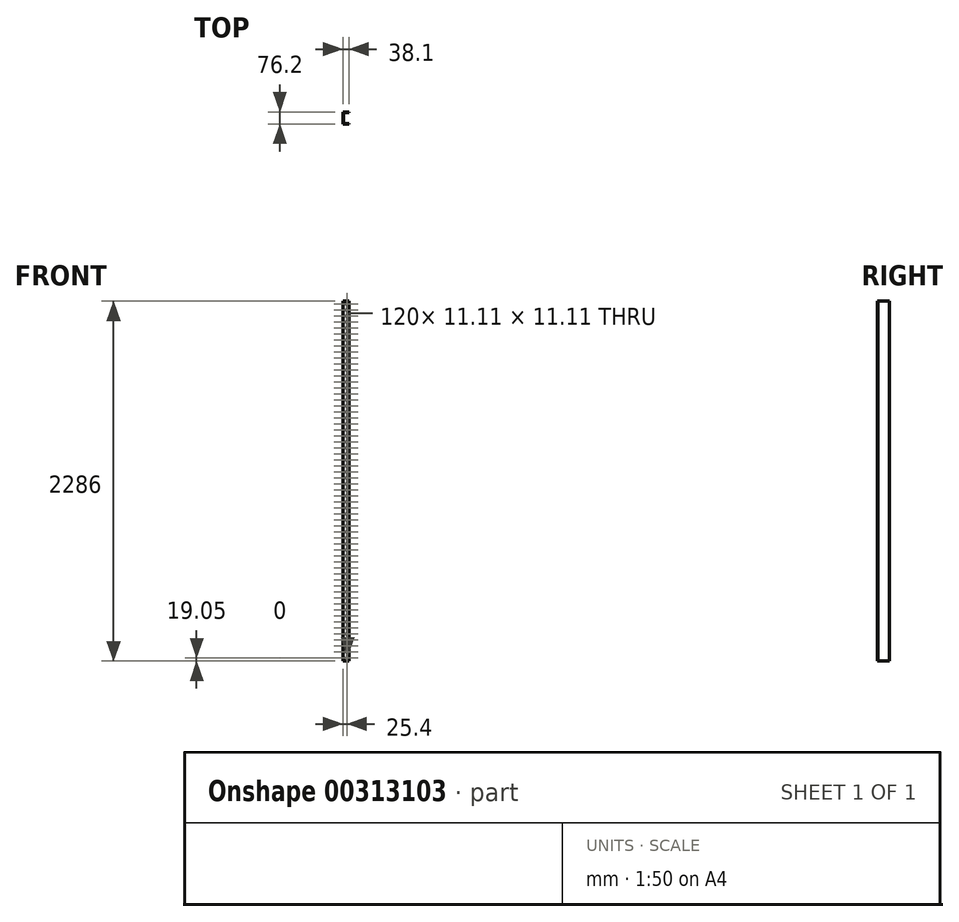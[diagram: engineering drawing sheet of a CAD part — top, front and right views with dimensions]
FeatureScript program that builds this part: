
annotation { "Feature Type Name" : "Feature", "Feature Type Description" : "" }
export const myFeature = defineFeature(function(context is Context, id is Id, definition is map)
    precondition{}
    {
        {
            var Q0;
            Q0=qCreatedBy(makeId("Top.planeOp"),FACE);
            var sketch = newSketch(context, id + "F0", { "sketchPlane" : qUnion([Q0])});
            skLineSegment(sketch, "E0.bottom", {"start": v(0, 0) * mm, "end": v(38.1, 0) * mm});
            skLineSegment(sketch, "E0.top", {"start": v(0, 76.2) * mm, "end": v(38.1, 76.2) * mm});
            skLineSegment(sketch, "E0.left", {"start": v(0, 0) * mm, "end": v(0, 76.2) * mm});
            skLineSegment(sketch, "E0.right", {"start": v(38.1, 0) * mm, "end": v(38.1, 76.2) * mm});
            skSolve(sketch);
        }
        {
            var Q0;
            Q0 = qSketchRegion(id + "F0", true);
            extrude(context, id + "F1", {"entities" : qUnion([Q0]), "endBound" : BoundingType.SYMMETRIC, "depth" : 2286 * mm});
        }
        {
            var Q0;
            Q0=makeQuery(id+"F1.opExtrude","SWEPT_FACE",FACE,{"disambiguationData":[OSD([sQuery(id+"F0.wireOp",EDGE,"E0.right")])]});
            var Q1;
            Q1=makeQuery(id+"F1.opExtrude","CAP_FACE",FACE,{"disambiguationData":[OSD([sQuery(id+"F0.wireOp",EDGE,"E0.bottom"),sQuery(id+"F0.wireOp",EDGE,"E0.top"),sQuery(id+"F0.wireOp",EDGE,"E0.left"),sQuery(id+"F0.wireOp",EDGE,"E0.right")])],"isStart":false});
            var Q2;
            Q2=makeQuery(id+"F1.opExtrude","CAP_FACE",FACE,{"disambiguationData":[OSD([sQuery(id+"F0.wireOp",EDGE,"E0.bottom"),sQuery(id+"F0.wireOp",EDGE,"E0.top"),sQuery(id+"F0.wireOp",EDGE,"E0.left"),sQuery(id+"F0.wireOp",EDGE,"E0.right")])],"isStart":true});
            shell(context, id + "F2", {"entities" : qUnion([Q0, Q1, Q2]), "thickness" : 2.78 * mm});
        }
        {
            var Q0;
            Q0=makeQuery(id+"F1.opExtrude","SWEPT_FACE",FACE,{"disambiguationData":[OSD([sQuery(id+"F0.wireOp",EDGE,"E0.bottom")])]});
            var sketch = newSketch(context, id + "F3", { "sketchPlane" : qUnion([Q0])});
            skLineSegment(sketch, "E1.bottom", {"start": v(30.96, -1118.4) * mm, "end": v(19.84, -1118.4) * mm});
            skLineSegment(sketch, "E1.top", {"start": v(30.96, -1129.5) * mm, "end": v(19.84, -1129.5) * mm});
            skLineSegment(sketch, "E1.left", {"start": v(30.96, -1118.4) * mm, "end": v(30.96, -1129.5) * mm});
            skLineSegment(sketch, "E1.right", {"start": v(19.84, -1118.4) * mm, "end": v(19.84, -1129.5) * mm});
            skPoint(sketch, "E1.middle", {"position": v(25.4, -1123.95) * mm});
            skPoint(sketch, "E1.middle.positionSnap0", {"position": v(19.05, -1143) * mm});
            skPoint(sketch, "E1.centerSnap0", {"position": v(19.05, -1143) * mm});
            skPoint(sketch, "E2.0.1.0", {"position": v(25.4, -1085.85) * mm});
            skLineSegment(sketch, "E2.0.1.1", {"start": v(19.84, -1080.3) * mm, "end": v(19.84, -1091.4) * mm});
            skLineSegment(sketch, "E2.0.1.2", {"start": v(30.96, -1080.3) * mm, "end": v(30.96, -1091.4) * mm});
            skLineSegment(sketch, "E2.0.1.3", {"start": v(30.96, -1091.4) * mm, "end": v(19.84, -1091.4) * mm});
            skLineSegment(sketch, "E2.0.1.4", {"start": v(30.96, -1080.3) * mm, "end": v(19.84, -1080.3) * mm});
            skPoint(sketch, "E2.0.2.0", {"position": v(25.4, -1047.75) * mm});
            skLineSegment(sketch, "E2.0.2.1", {"start": v(19.84, -1042.2) * mm, "end": v(19.84, -1053.3) * mm});
            skLineSegment(sketch, "E2.0.2.2", {"start": v(30.96, -1042.2) * mm, "end": v(30.96, -1053.3) * mm});
            skLineSegment(sketch, "E2.0.2.3", {"start": v(30.96, -1053.3) * mm, "end": v(19.84, -1053.3) * mm});
            skLineSegment(sketch, "E2.0.2.4", {"start": v(30.96, -1042.2) * mm, "end": v(19.84, -1042.2) * mm});
            skPoint(sketch, "E2.0.3.0", {"position": v(25.4, -1009.65) * mm});
            skLineSegment(sketch, "E2.0.3.1", {"start": v(19.84, -1004.1) * mm, "end": v(19.84, -1015.2) * mm});
            skLineSegment(sketch, "E2.0.3.2", {"start": v(30.96, -1004.1) * mm, "end": v(30.96, -1015.2) * mm});
            skLineSegment(sketch, "E2.0.3.3", {"start": v(30.96, -1015.2) * mm, "end": v(19.84, -1015.2) * mm});
            skLineSegment(sketch, "E2.0.3.4", {"start": v(30.96, -1004.1) * mm, "end": v(19.84, -1004.1) * mm});
            skPoint(sketch, "E2.0.4.0", {"position": v(25.4, -971.55) * mm});
            skLineSegment(sketch, "E2.0.4.1", {"start": v(19.84, -966) * mm, "end": v(19.84, -977.1) * mm});
            skLineSegment(sketch, "E2.0.4.2", {"start": v(30.96, -966) * mm, "end": v(30.96, -977.1) * mm});
            skLineSegment(sketch, "E2.0.4.3", {"start": v(30.96, -977.1) * mm, "end": v(19.84, -977.1) * mm});
            skLineSegment(sketch, "E2.0.4.4", {"start": v(30.96, -966) * mm, "end": v(19.84, -966) * mm});
            skPoint(sketch, "E2.0.5.0", {"position": v(25.4, -933.45) * mm});
            skLineSegment(sketch, "E2.0.5.1", {"start": v(19.84, -927.9) * mm, "end": v(19.84, -939) * mm});
            skLineSegment(sketch, "E2.0.5.2", {"start": v(30.96, -927.9) * mm, "end": v(30.96, -939) * mm});
            skLineSegment(sketch, "E2.0.5.3", {"start": v(30.96, -939) * mm, "end": v(19.84, -939) * mm});
            skLineSegment(sketch, "E2.0.5.4", {"start": v(30.96, -927.9) * mm, "end": v(19.84, -927.9) * mm});
            skPoint(sketch, "E2.0.6.0", {"position": v(25.4, -895.35) * mm});
            skLineSegment(sketch, "E2.0.6.1", {"start": v(19.84, -889.8) * mm, "end": v(19.84, -900.9) * mm});
            skLineSegment(sketch, "E2.0.6.2", {"start": v(30.96, -889.8) * mm, "end": v(30.96, -900.9) * mm});
            skLineSegment(sketch, "E2.0.6.3", {"start": v(30.96, -900.9) * mm, "end": v(19.84, -900.9) * mm});
            skLineSegment(sketch, "E2.0.6.4", {"start": v(30.96, -889.8) * mm, "end": v(19.84, -889.8) * mm});
            skPoint(sketch, "E2.0.7.0", {"position": v(25.4, -857.25) * mm});
            skLineSegment(sketch, "E2.0.7.1", {"start": v(19.84, -851.7) * mm, "end": v(19.84, -862.8) * mm});
            skLineSegment(sketch, "E2.0.7.2", {"start": v(30.96, -851.7) * mm, "end": v(30.96, -862.8) * mm});
            skLineSegment(sketch, "E2.0.7.3", {"start": v(30.96, -862.8) * mm, "end": v(19.84, -862.8) * mm});
            skLineSegment(sketch, "E2.0.7.4", {"start": v(30.96, -851.7) * mm, "end": v(19.84, -851.7) * mm});
            skPoint(sketch, "E2.0.8.0", {"position": v(25.4, -819.15) * mm});
            skLineSegment(sketch, "E2.0.8.1", {"start": v(19.84, -813.6) * mm, "end": v(19.84, -824.7) * mm});
            skLineSegment(sketch, "E2.0.8.2", {"start": v(30.96, -813.6) * mm, "end": v(30.96, -824.7) * mm});
            skLineSegment(sketch, "E2.0.8.3", {"start": v(30.96, -824.7) * mm, "end": v(19.84, -824.7) * mm});
            skLineSegment(sketch, "E2.0.8.4", {"start": v(30.96, -813.6) * mm, "end": v(19.84, -813.6) * mm});
            skPoint(sketch, "E2.0.9.0", {"position": v(25.4, -781.05) * mm});
            skLineSegment(sketch, "E2.0.9.1", {"start": v(19.84, -775.5) * mm, "end": v(19.84, -786.6) * mm});
            skLineSegment(sketch, "E2.0.9.2", {"start": v(30.96, -775.5) * mm, "end": v(30.96, -786.6) * mm});
            skLineSegment(sketch, "E2.0.9.3", {"start": v(30.96, -786.6) * mm, "end": v(19.84, -786.6) * mm});
            skLineSegment(sketch, "E2.0.9.4", {"start": v(30.96, -775.5) * mm, "end": v(19.84, -775.5) * mm});
            skPoint(sketch, "E2.0.10.0", {"position": v(25.4, -742.95) * mm});
            skLineSegment(sketch, "E2.0.10.1", {"start": v(19.84, -737.4) * mm, "end": v(19.84, -748.5) * mm});
            skLineSegment(sketch, "E2.0.10.2", {"start": v(30.96, -737.4) * mm, "end": v(30.96, -748.5) * mm});
            skLineSegment(sketch, "E2.0.10.3", {"start": v(30.96, -748.5) * mm, "end": v(19.84, -748.5) * mm});
            skLineSegment(sketch, "E2.0.10.4", {"start": v(30.96, -737.4) * mm, "end": v(19.84, -737.4) * mm});
            skPoint(sketch, "E2.0.11.0", {"position": v(25.4, -704.85) * mm});
            skLineSegment(sketch, "E2.0.11.1", {"start": v(19.84, -699.3) * mm, "end": v(19.84, -710.4) * mm});
            skLineSegment(sketch, "E2.0.11.2", {"start": v(30.96, -699.3) * mm, "end": v(30.96, -710.4) * mm});
            skLineSegment(sketch, "E2.0.11.3", {"start": v(30.96, -710.4) * mm, "end": v(19.84, -710.4) * mm});
            skLineSegment(sketch, "E2.0.11.4", {"start": v(30.96, -699.3) * mm, "end": v(19.84, -699.3) * mm});
            skPoint(sketch, "E2.0.12.0", {"position": v(25.4, -666.75) * mm});
            skLineSegment(sketch, "E2.0.12.1", {"start": v(19.84, -661.2) * mm, "end": v(19.84, -672.3) * mm});
            skLineSegment(sketch, "E2.0.12.2", {"start": v(30.96, -661.2) * mm, "end": v(30.96, -672.3) * mm});
            skLineSegment(sketch, "E2.0.12.3", {"start": v(30.96, -672.3) * mm, "end": v(19.84, -672.3) * mm});
            skLineSegment(sketch, "E2.0.12.4", {"start": v(30.96, -661.2) * mm, "end": v(19.84, -661.2) * mm});
            skPoint(sketch, "E2.0.13.0", {"position": v(25.4, -628.65) * mm});
            skLineSegment(sketch, "E2.0.13.1", {"start": v(19.84, -623.1) * mm, "end": v(19.84, -634.2) * mm});
            skLineSegment(sketch, "E2.0.13.2", {"start": v(30.96, -623.1) * mm, "end": v(30.96, -634.2) * mm});
            skLineSegment(sketch, "E2.0.13.3", {"start": v(30.96, -634.2) * mm, "end": v(19.84, -634.2) * mm});
            skLineSegment(sketch, "E2.0.13.4", {"start": v(30.96, -623.1) * mm, "end": v(19.84, -623.1) * mm});
            skPoint(sketch, "E2.0.14.0", {"position": v(25.4, -590.55) * mm});
            skLineSegment(sketch, "E2.0.14.1", {"start": v(19.84, -585) * mm, "end": v(19.84, -596.1) * mm});
            skLineSegment(sketch, "E2.0.14.2", {"start": v(30.96, -585) * mm, "end": v(30.96, -596.1) * mm});
            skLineSegment(sketch, "E2.0.14.3", {"start": v(30.96, -596.1) * mm, "end": v(19.84, -596.1) * mm});
            skLineSegment(sketch, "E2.0.14.4", {"start": v(30.96, -585) * mm, "end": v(19.84, -585) * mm});
            skPoint(sketch, "E2.0.15.0", {"position": v(25.4, -552.45) * mm});
            skLineSegment(sketch, "E2.0.15.1", {"start": v(19.84, -546.9) * mm, "end": v(19.84, -558) * mm});
            skLineSegment(sketch, "E2.0.15.2", {"start": v(30.96, -546.9) * mm, "end": v(30.96, -558) * mm});
            skLineSegment(sketch, "E2.0.15.3", {"start": v(30.96, -558) * mm, "end": v(19.84, -558) * mm});
            skLineSegment(sketch, "E2.0.15.4", {"start": v(30.96, -546.9) * mm, "end": v(19.84, -546.9) * mm});
            skPoint(sketch, "E2.0.16.0", {"position": v(25.4, -514.35) * mm});
            skLineSegment(sketch, "E2.0.16.1", {"start": v(19.84, -508.8) * mm, "end": v(19.84, -519.9) * mm});
            skLineSegment(sketch, "E2.0.16.2", {"start": v(30.96, -508.8) * mm, "end": v(30.96, -519.9) * mm});
            skLineSegment(sketch, "E2.0.16.3", {"start": v(30.96, -519.9) * mm, "end": v(19.84, -519.9) * mm});
            skLineSegment(sketch, "E2.0.16.4", {"start": v(30.96, -508.8) * mm, "end": v(19.84, -508.8) * mm});
            skPoint(sketch, "E2.0.17.0", {"position": v(25.4, -476.25) * mm});
            skLineSegment(sketch, "E2.0.17.1", {"start": v(19.84, -470.7) * mm, "end": v(19.84, -481.8) * mm});
            skLineSegment(sketch, "E2.0.17.2", {"start": v(30.96, -470.7) * mm, "end": v(30.96, -481.8) * mm});
            skLineSegment(sketch, "E2.0.17.3", {"start": v(30.96, -481.8) * mm, "end": v(19.84, -481.8) * mm});
            skLineSegment(sketch, "E2.0.17.4", {"start": v(30.96, -470.7) * mm, "end": v(19.84, -470.7) * mm});
            skPoint(sketch, "E2.0.18.0", {"position": v(25.4, -438.15) * mm});
            skLineSegment(sketch, "E2.0.18.1", {"start": v(19.84, -432.6) * mm, "end": v(19.84, -443.7) * mm});
            skLineSegment(sketch, "E2.0.18.2", {"start": v(30.96, -432.6) * mm, "end": v(30.96, -443.7) * mm});
            skLineSegment(sketch, "E2.0.18.3", {"start": v(30.96, -443.7) * mm, "end": v(19.84, -443.7) * mm});
            skLineSegment(sketch, "E2.0.18.4", {"start": v(30.96, -432.6) * mm, "end": v(19.84, -432.6) * mm});
            skPoint(sketch, "E2.0.19.0", {"position": v(25.4, -400.05) * mm});
            skLineSegment(sketch, "E2.0.19.1", {"start": v(19.84, -394.5) * mm, "end": v(19.84, -405.6) * mm});
            skLineSegment(sketch, "E2.0.19.2", {"start": v(30.96, -394.5) * mm, "end": v(30.96, -405.6) * mm});
            skLineSegment(sketch, "E2.0.19.3", {"start": v(30.96, -405.6) * mm, "end": v(19.84, -405.6) * mm});
            skLineSegment(sketch, "E2.0.19.4", {"start": v(30.96, -394.5) * mm, "end": v(19.84, -394.5) * mm});
            skPoint(sketch, "E2.0.20.0", {"position": v(25.4, -361.95) * mm});
            skLineSegment(sketch, "E2.0.20.1", {"start": v(19.84, -356.4) * mm, "end": v(19.84, -367.5) * mm});
            skLineSegment(sketch, "E2.0.20.2", {"start": v(30.96, -356.4) * mm, "end": v(30.96, -367.5) * mm});
            skLineSegment(sketch, "E2.0.20.3", {"start": v(30.96, -367.5) * mm, "end": v(19.84, -367.5) * mm});
            skLineSegment(sketch, "E2.0.20.4", {"start": v(30.96, -356.4) * mm, "end": v(19.84, -356.4) * mm});
            skPoint(sketch, "E2.0.21.0", {"position": v(25.4, -323.85) * mm});
            skLineSegment(sketch, "E2.0.21.1", {"start": v(19.84, -318.3) * mm, "end": v(19.84, -329.4) * mm});
            skLineSegment(sketch, "E2.0.21.2", {"start": v(30.96, -318.3) * mm, "end": v(30.96, -329.4) * mm});
            skLineSegment(sketch, "E2.0.21.3", {"start": v(30.96, -329.4) * mm, "end": v(19.84, -329.4) * mm});
            skLineSegment(sketch, "E2.0.21.4", {"start": v(30.96, -318.3) * mm, "end": v(19.84, -318.3) * mm});
            skPoint(sketch, "E2.0.22.0", {"position": v(25.4, -285.75) * mm});
            skLineSegment(sketch, "E2.0.22.1", {"start": v(19.84, -280.2) * mm, "end": v(19.84, -291.3) * mm});
            skLineSegment(sketch, "E2.0.22.2", {"start": v(30.96, -280.2) * mm, "end": v(30.96, -291.3) * mm});
            skLineSegment(sketch, "E2.0.22.3", {"start": v(30.96, -291.3) * mm, "end": v(19.84, -291.3) * mm});
            skLineSegment(sketch, "E2.0.22.4", {"start": v(30.96, -280.2) * mm, "end": v(19.84, -280.2) * mm});
            skPoint(sketch, "E2.0.23.0", {"position": v(25.4, -247.65) * mm});
            skLineSegment(sketch, "E2.0.23.1", {"start": v(19.84, -242.1) * mm, "end": v(19.84, -253.2) * mm});
            skLineSegment(sketch, "E2.0.23.2", {"start": v(30.96, -242.1) * mm, "end": v(30.96, -253.2) * mm});
            skLineSegment(sketch, "E2.0.23.3", {"start": v(30.96, -253.2) * mm, "end": v(19.84, -253.2) * mm});
            skLineSegment(sketch, "E2.0.23.4", {"start": v(30.96, -242.1) * mm, "end": v(19.84, -242.1) * mm});
            skPoint(sketch, "E2.0.24.0", {"position": v(25.4, -209.55) * mm});
            skLineSegment(sketch, "E2.0.24.1", {"start": v(19.84, -204) * mm, "end": v(19.84, -215.1) * mm});
            skLineSegment(sketch, "E2.0.24.2", {"start": v(30.96, -204) * mm, "end": v(30.96, -215.1) * mm});
            skLineSegment(sketch, "E2.0.24.3", {"start": v(30.96, -215.1) * mm, "end": v(19.84, -215.1) * mm});
            skLineSegment(sketch, "E2.0.24.4", {"start": v(30.96, -204) * mm, "end": v(19.84, -204) * mm});
            skPoint(sketch, "E2.0.25.0", {"position": v(25.4, -171.45) * mm});
            skLineSegment(sketch, "E2.0.25.1", {"start": v(19.84, -165.9) * mm, "end": v(19.84, -177) * mm});
            skLineSegment(sketch, "E2.0.25.2", {"start": v(30.96, -165.9) * mm, "end": v(30.96, -177) * mm});
            skLineSegment(sketch, "E2.0.25.3", {"start": v(30.96, -177) * mm, "end": v(19.84, -177) * mm});
            skLineSegment(sketch, "E2.0.25.4", {"start": v(30.96, -165.9) * mm, "end": v(19.84, -165.9) * mm});
            skPoint(sketch, "E2.0.26.0", {"position": v(25.4, -133.35) * mm});
            skLineSegment(sketch, "E2.0.26.1", {"start": v(19.84, -127.8) * mm, "end": v(19.84, -138.9) * mm});
            skLineSegment(sketch, "E2.0.26.2", {"start": v(30.96, -127.8) * mm, "end": v(30.96, -138.9) * mm});
            skLineSegment(sketch, "E2.0.26.3", {"start": v(30.96, -138.9) * mm, "end": v(19.84, -138.9) * mm});
            skLineSegment(sketch, "E2.0.26.4", {"start": v(30.96, -127.8) * mm, "end": v(19.84, -127.8) * mm});
            skPoint(sketch, "E2.0.27.0", {"position": v(25.4, -95.25) * mm});
            skLineSegment(sketch, "E2.0.27.1", {"start": v(19.84, -89.7) * mm, "end": v(19.84, -100.8) * mm});
            skLineSegment(sketch, "E2.0.27.2", {"start": v(30.96, -89.7) * mm, "end": v(30.96, -100.8) * mm});
            skLineSegment(sketch, "E2.0.27.3", {"start": v(30.96, -100.8) * mm, "end": v(19.84, -100.8) * mm});
            skLineSegment(sketch, "E2.0.27.4", {"start": v(30.96, -89.7) * mm, "end": v(19.84, -89.7) * mm});
            skPoint(sketch, "E2.0.28.0", {"position": v(25.4, -57.15) * mm});
            skLineSegment(sketch, "E2.0.28.1", {"start": v(19.84, -51.6) * mm, "end": v(19.84, -62.7) * mm});
            skLineSegment(sketch, "E2.0.28.2", {"start": v(30.96, -51.6) * mm, "end": v(30.96, -62.7) * mm});
            skLineSegment(sketch, "E2.0.28.3", {"start": v(30.96, -62.7) * mm, "end": v(19.84, -62.7) * mm});
            skLineSegment(sketch, "E2.0.28.4", {"start": v(30.96, -51.6) * mm, "end": v(19.84, -51.6) * mm});
            skPoint(sketch, "E2.0.29.0", {"position": v(25.4, -19.05) * mm});
            skLineSegment(sketch, "E2.0.29.1", {"start": v(19.84, -13.5) * mm, "end": v(19.84, -24.6) * mm});
            skLineSegment(sketch, "E2.0.29.2", {"start": v(30.96, -13.5) * mm, "end": v(30.96, -24.6) * mm});
            skLineSegment(sketch, "E2.0.29.3", {"start": v(30.96, -24.6) * mm, "end": v(19.84, -24.6) * mm});
            skLineSegment(sketch, "E2.0.29.4", {"start": v(30.96, -13.5) * mm, "end": v(19.84, -13.5) * mm});
            skPoint(sketch, "E2.0.30.0", {"position": v(25.4, 19.05) * mm});
            skLineSegment(sketch, "E2.0.30.1", {"start": v(19.84, 24.6) * mm, "end": v(19.84, 13.5) * mm});
            skLineSegment(sketch, "E2.0.30.2", {"start": v(30.96, 24.6) * mm, "end": v(30.96, 13.5) * mm});
            skLineSegment(sketch, "E2.0.30.3", {"start": v(30.96, 13.5) * mm, "end": v(19.84, 13.5) * mm});
            skLineSegment(sketch, "E2.0.30.4", {"start": v(30.96, 24.6) * mm, "end": v(19.84, 24.6) * mm});
            skPoint(sketch, "E2.0.31.0", {"position": v(25.4, 57.15) * mm});
            skLineSegment(sketch, "E2.0.31.1", {"start": v(19.84, 62.7) * mm, "end": v(19.84, 51.6) * mm});
            skLineSegment(sketch, "E2.0.31.2", {"start": v(30.96, 62.7) * mm, "end": v(30.96, 51.6) * mm});
            skLineSegment(sketch, "E2.0.31.3", {"start": v(30.96, 51.6) * mm, "end": v(19.84, 51.6) * mm});
            skLineSegment(sketch, "E2.0.31.4", {"start": v(30.96, 62.7) * mm, "end": v(19.84, 62.7) * mm});
            skPoint(sketch, "E2.0.32.0", {"position": v(25.4, 95.25) * mm});
            skLineSegment(sketch, "E2.0.32.1", {"start": v(19.84, 100.8) * mm, "end": v(19.84, 89.7) * mm});
            skLineSegment(sketch, "E2.0.32.2", {"start": v(30.96, 100.8) * mm, "end": v(30.96, 89.7) * mm});
            skLineSegment(sketch, "E2.0.32.3", {"start": v(30.96, 89.7) * mm, "end": v(19.84, 89.7) * mm});
            skLineSegment(sketch, "E2.0.32.4", {"start": v(30.96, 100.8) * mm, "end": v(19.84, 100.8) * mm});
            skPoint(sketch, "E2.0.33.0", {"position": v(25.4, 133.35) * mm});
            skLineSegment(sketch, "E2.0.33.1", {"start": v(19.84, 138.9) * mm, "end": v(19.84, 127.8) * mm});
            skLineSegment(sketch, "E2.0.33.2", {"start": v(30.96, 138.9) * mm, "end": v(30.96, 127.8) * mm});
            skLineSegment(sketch, "E2.0.33.3", {"start": v(30.96, 127.8) * mm, "end": v(19.84, 127.8) * mm});
            skLineSegment(sketch, "E2.0.33.4", {"start": v(30.96, 138.9) * mm, "end": v(19.84, 138.9) * mm});
            skPoint(sketch, "E2.0.34.0", {"position": v(25.4, 171.45) * mm});
            skLineSegment(sketch, "E2.0.34.1", {"start": v(19.84, 177) * mm, "end": v(19.84, 165.9) * mm});
            skLineSegment(sketch, "E2.0.34.2", {"start": v(30.96, 177) * mm, "end": v(30.96, 165.9) * mm});
            skLineSegment(sketch, "E2.0.34.3", {"start": v(30.96, 165.9) * mm, "end": v(19.84, 165.9) * mm});
            skLineSegment(sketch, "E2.0.34.4", {"start": v(30.96, 177) * mm, "end": v(19.84, 177) * mm});
            skPoint(sketch, "E2.0.35.0", {"position": v(25.4, 209.55) * mm});
            skLineSegment(sketch, "E2.0.35.1", {"start": v(19.84, 215.1) * mm, "end": v(19.84, 204) * mm});
            skLineSegment(sketch, "E2.0.35.2", {"start": v(30.96, 215.1) * mm, "end": v(30.96, 204) * mm});
            skLineSegment(sketch, "E2.0.35.3", {"start": v(30.96, 204) * mm, "end": v(19.84, 204) * mm});
            skLineSegment(sketch, "E2.0.35.4", {"start": v(30.96, 215.1) * mm, "end": v(19.84, 215.1) * mm});
            skPoint(sketch, "E2.0.36.0", {"position": v(25.4, 247.65) * mm});
            skLineSegment(sketch, "E2.0.36.1", {"start": v(19.84, 253.2) * mm, "end": v(19.84, 242.1) * mm});
            skLineSegment(sketch, "E2.0.36.2", {"start": v(30.96, 253.2) * mm, "end": v(30.96, 242.1) * mm});
            skLineSegment(sketch, "E2.0.36.3", {"start": v(30.96, 242.1) * mm, "end": v(19.84, 242.1) * mm});
            skLineSegment(sketch, "E2.0.36.4", {"start": v(30.96, 253.2) * mm, "end": v(19.84, 253.2) * mm});
            skPoint(sketch, "E2.0.37.0", {"position": v(25.4, 285.75) * mm});
            skLineSegment(sketch, "E2.0.37.1", {"start": v(19.84, 291.3) * mm, "end": v(19.84, 280.2) * mm});
            skLineSegment(sketch, "E2.0.37.2", {"start": v(30.96, 291.3) * mm, "end": v(30.96, 280.2) * mm});
            skLineSegment(sketch, "E2.0.37.3", {"start": v(30.96, 280.2) * mm, "end": v(19.84, 280.2) * mm});
            skLineSegment(sketch, "E2.0.37.4", {"start": v(30.96, 291.3) * mm, "end": v(19.84, 291.3) * mm});
            skPoint(sketch, "E2.0.38.0", {"position": v(25.4, 323.85) * mm});
            skLineSegment(sketch, "E2.0.38.1", {"start": v(19.84, 329.4) * mm, "end": v(19.84, 318.3) * mm});
            skLineSegment(sketch, "E2.0.38.2", {"start": v(30.96, 329.4) * mm, "end": v(30.96, 318.3) * mm});
            skLineSegment(sketch, "E2.0.38.3", {"start": v(30.96, 318.3) * mm, "end": v(19.84, 318.3) * mm});
            skLineSegment(sketch, "E2.0.38.4", {"start": v(30.96, 329.4) * mm, "end": v(19.84, 329.4) * mm});
            skPoint(sketch, "E2.0.39.0", {"position": v(25.4, 361.95) * mm});
            skLineSegment(sketch, "E2.0.39.1", {"start": v(19.84, 367.5) * mm, "end": v(19.84, 356.4) * mm});
            skLineSegment(sketch, "E2.0.39.2", {"start": v(30.96, 367.5) * mm, "end": v(30.96, 356.4) * mm});
            skLineSegment(sketch, "E2.0.39.3", {"start": v(30.96, 356.4) * mm, "end": v(19.84, 356.4) * mm});
            skLineSegment(sketch, "E2.0.39.4", {"start": v(30.96, 367.5) * mm, "end": v(19.84, 367.5) * mm});
            skPoint(sketch, "E2.0.40.0", {"position": v(25.4, 400.05) * mm});
            skLineSegment(sketch, "E2.0.40.1", {"start": v(19.84, 405.6) * mm, "end": v(19.84, 394.5) * mm});
            skLineSegment(sketch, "E2.0.40.2", {"start": v(30.96, 405.6) * mm, "end": v(30.96, 394.5) * mm});
            skLineSegment(sketch, "E2.0.40.3", {"start": v(30.96, 394.5) * mm, "end": v(19.84, 394.5) * mm});
            skLineSegment(sketch, "E2.0.40.4", {"start": v(30.96, 405.6) * mm, "end": v(19.84, 405.6) * mm});
            skPoint(sketch, "E2.0.41.0", {"position": v(25.4, 438.15) * mm});
            skLineSegment(sketch, "E2.0.41.1", {"start": v(19.84, 443.7) * mm, "end": v(19.84, 432.6) * mm});
            skLineSegment(sketch, "E2.0.41.2", {"start": v(30.96, 443.7) * mm, "end": v(30.96, 432.6) * mm});
            skLineSegment(sketch, "E2.0.41.3", {"start": v(30.96, 432.6) * mm, "end": v(19.84, 432.6) * mm});
            skLineSegment(sketch, "E2.0.41.4", {"start": v(30.96, 443.7) * mm, "end": v(19.84, 443.7) * mm});
            skPoint(sketch, "E2.0.42.0", {"position": v(25.4, 476.25) * mm});
            skLineSegment(sketch, "E2.0.42.1", {"start": v(19.84, 481.8) * mm, "end": v(19.84, 470.7) * mm});
            skLineSegment(sketch, "E2.0.42.2", {"start": v(30.96, 481.8) * mm, "end": v(30.96, 470.7) * mm});
            skLineSegment(sketch, "E2.0.42.3", {"start": v(30.96, 470.7) * mm, "end": v(19.84, 470.7) * mm});
            skLineSegment(sketch, "E2.0.42.4", {"start": v(30.96, 481.8) * mm, "end": v(19.84, 481.8) * mm});
            skPoint(sketch, "E2.0.43.0", {"position": v(25.4, 514.35) * mm});
            skLineSegment(sketch, "E2.0.43.1", {"start": v(19.84, 519.9) * mm, "end": v(19.84, 508.8) * mm});
            skLineSegment(sketch, "E2.0.43.2", {"start": v(30.96, 519.9) * mm, "end": v(30.96, 508.8) * mm});
            skLineSegment(sketch, "E2.0.43.3", {"start": v(30.96, 508.8) * mm, "end": v(19.84, 508.8) * mm});
            skLineSegment(sketch, "E2.0.43.4", {"start": v(30.96, 519.9) * mm, "end": v(19.84, 519.9) * mm});
            skPoint(sketch, "E2.0.44.0", {"position": v(25.4, 552.45) * mm});
            skLineSegment(sketch, "E2.0.44.1", {"start": v(19.84, 558) * mm, "end": v(19.84, 546.9) * mm});
            skLineSegment(sketch, "E2.0.44.2", {"start": v(30.96, 558) * mm, "end": v(30.96, 546.9) * mm});
            skLineSegment(sketch, "E2.0.44.3", {"start": v(30.96, 546.9) * mm, "end": v(19.84, 546.9) * mm});
            skLineSegment(sketch, "E2.0.44.4", {"start": v(30.96, 558) * mm, "end": v(19.84, 558) * mm});
            skPoint(sketch, "E2.0.45.0", {"position": v(25.4, 590.55) * mm});
            skLineSegment(sketch, "E2.0.45.1", {"start": v(19.84, 596.1) * mm, "end": v(19.84, 585) * mm});
            skLineSegment(sketch, "E2.0.45.2", {"start": v(30.96, 596.1) * mm, "end": v(30.96, 585) * mm});
            skLineSegment(sketch, "E2.0.45.3", {"start": v(30.96, 585) * mm, "end": v(19.84, 585) * mm});
            skLineSegment(sketch, "E2.0.45.4", {"start": v(30.96, 596.1) * mm, "end": v(19.84, 596.1) * mm});
            skPoint(sketch, "E2.0.46.0", {"position": v(25.4, 628.65) * mm});
            skLineSegment(sketch, "E2.0.46.1", {"start": v(19.84, 634.2) * mm, "end": v(19.84, 623.1) * mm});
            skLineSegment(sketch, "E2.0.46.2", {"start": v(30.96, 634.2) * mm, "end": v(30.96, 623.1) * mm});
            skLineSegment(sketch, "E2.0.46.3", {"start": v(30.96, 623.1) * mm, "end": v(19.84, 623.1) * mm});
            skLineSegment(sketch, "E2.0.46.4", {"start": v(30.96, 634.2) * mm, "end": v(19.84, 634.2) * mm});
            skPoint(sketch, "E2.0.47.0", {"position": v(25.4, 666.75) * mm});
            skLineSegment(sketch, "E2.0.47.1", {"start": v(19.84, 672.3) * mm, "end": v(19.84, 661.2) * mm});
            skLineSegment(sketch, "E2.0.47.2", {"start": v(30.96, 672.3) * mm, "end": v(30.96, 661.2) * mm});
            skLineSegment(sketch, "E2.0.47.3", {"start": v(30.96, 661.2) * mm, "end": v(19.84, 661.2) * mm});
            skLineSegment(sketch, "E2.0.47.4", {"start": v(30.96, 672.3) * mm, "end": v(19.84, 672.3) * mm});
            skPoint(sketch, "E2.0.48.0", {"position": v(25.4, 704.85) * mm});
            skLineSegment(sketch, "E2.0.48.1", {"start": v(19.84, 710.4) * mm, "end": v(19.84, 699.3) * mm});
            skLineSegment(sketch, "E2.0.48.2", {"start": v(30.96, 710.4) * mm, "end": v(30.96, 699.3) * mm});
            skLineSegment(sketch, "E2.0.48.3", {"start": v(30.96, 699.3) * mm, "end": v(19.84, 699.3) * mm});
            skLineSegment(sketch, "E2.0.48.4", {"start": v(30.96, 710.4) * mm, "end": v(19.84, 710.4) * mm});
            skPoint(sketch, "E2.0.49.0", {"position": v(25.4, 742.95) * mm});
            skLineSegment(sketch, "E2.0.49.1", {"start": v(19.84, 748.5) * mm, "end": v(19.84, 737.4) * mm});
            skLineSegment(sketch, "E2.0.49.2", {"start": v(30.96, 748.5) * mm, "end": v(30.96, 737.4) * mm});
            skLineSegment(sketch, "E2.0.49.3", {"start": v(30.96, 737.4) * mm, "end": v(19.84, 737.4) * mm});
            skLineSegment(sketch, "E2.0.49.4", {"start": v(30.96, 748.5) * mm, "end": v(19.84, 748.5) * mm});
            skPoint(sketch, "E2.0.50.0", {"position": v(25.4, 781.05) * mm});
            skLineSegment(sketch, "E2.0.50.1", {"start": v(19.84, 786.6) * mm, "end": v(19.84, 775.5) * mm});
            skLineSegment(sketch, "E2.0.50.2", {"start": v(30.96, 786.6) * mm, "end": v(30.96, 775.5) * mm});
            skLineSegment(sketch, "E2.0.50.3", {"start": v(30.96, 775.5) * mm, "end": v(19.84, 775.5) * mm});
            skLineSegment(sketch, "E2.0.50.4", {"start": v(30.96, 786.6) * mm, "end": v(19.84, 786.6) * mm});
            skPoint(sketch, "E2.0.51.0", {"position": v(25.4, 819.15) * mm});
            skLineSegment(sketch, "E2.0.51.1", {"start": v(19.84, 824.7) * mm, "end": v(19.84, 813.6) * mm});
            skLineSegment(sketch, "E2.0.51.2", {"start": v(30.96, 824.7) * mm, "end": v(30.96, 813.6) * mm});
            skLineSegment(sketch, "E2.0.51.3", {"start": v(30.96, 813.6) * mm, "end": v(19.84, 813.6) * mm});
            skLineSegment(sketch, "E2.0.51.4", {"start": v(30.96, 824.7) * mm, "end": v(19.84, 824.7) * mm});
            skPoint(sketch, "E2.0.52.0", {"position": v(25.4, 857.25) * mm});
            skLineSegment(sketch, "E2.0.52.1", {"start": v(19.84, 862.8) * mm, "end": v(19.84, 851.7) * mm});
            skLineSegment(sketch, "E2.0.52.2", {"start": v(30.96, 862.8) * mm, "end": v(30.96, 851.7) * mm});
            skLineSegment(sketch, "E2.0.52.3", {"start": v(30.96, 851.7) * mm, "end": v(19.84, 851.7) * mm});
            skLineSegment(sketch, "E2.0.52.4", {"start": v(30.96, 862.8) * mm, "end": v(19.84, 862.8) * mm});
            skPoint(sketch, "E2.0.53.0", {"position": v(25.4, 895.35) * mm});
            skLineSegment(sketch, "E2.0.53.1", {"start": v(19.84, 900.9) * mm, "end": v(19.84, 889.8) * mm});
            skLineSegment(sketch, "E2.0.53.2", {"start": v(30.96, 900.9) * mm, "end": v(30.96, 889.8) * mm});
            skLineSegment(sketch, "E2.0.53.3", {"start": v(30.96, 889.8) * mm, "end": v(19.84, 889.8) * mm});
            skLineSegment(sketch, "E2.0.53.4", {"start": v(30.96, 900.9) * mm, "end": v(19.84, 900.9) * mm});
            skPoint(sketch, "E2.0.54.0", {"position": v(25.4, 933.45) * mm});
            skLineSegment(sketch, "E2.0.54.1", {"start": v(19.84, 939) * mm, "end": v(19.84, 927.9) * mm});
            skLineSegment(sketch, "E2.0.54.2", {"start": v(30.96, 939) * mm, "end": v(30.96, 927.9) * mm});
            skLineSegment(sketch, "E2.0.54.3", {"start": v(30.96, 927.9) * mm, "end": v(19.84, 927.9) * mm});
            skLineSegment(sketch, "E2.0.54.4", {"start": v(30.96, 939) * mm, "end": v(19.84, 939) * mm});
            skPoint(sketch, "E2.0.55.0", {"position": v(25.4, 971.55) * mm});
            skLineSegment(sketch, "E2.0.55.1", {"start": v(19.84, 977.1) * mm, "end": v(19.84, 966) * mm});
            skLineSegment(sketch, "E2.0.55.2", {"start": v(30.96, 977.1) * mm, "end": v(30.96, 966) * mm});
            skLineSegment(sketch, "E2.0.55.3", {"start": v(30.96, 966) * mm, "end": v(19.84, 966) * mm});
            skLineSegment(sketch, "E2.0.55.4", {"start": v(30.96, 977.1) * mm, "end": v(19.84, 977.1) * mm});
            skPoint(sketch, "E2.0.56.0", {"position": v(25.4, 1009.65) * mm});
            skLineSegment(sketch, "E2.0.56.1", {"start": v(19.84, 1015.2) * mm, "end": v(19.84, 1004.1) * mm});
            skLineSegment(sketch, "E2.0.56.2", {"start": v(30.96, 1015.2) * mm, "end": v(30.96, 1004.1) * mm});
            skLineSegment(sketch, "E2.0.56.3", {"start": v(30.96, 1004.1) * mm, "end": v(19.84, 1004.1) * mm});
            skLineSegment(sketch, "E2.0.56.4", {"start": v(30.96, 1015.2) * mm, "end": v(19.84, 1015.2) * mm});
            skLineSegment(sketch, "E2.direction1", {"start": v(19.84, -1129.5) * mm, "end": v(38.9, -1129.5) * mm, "construction": true});
            skLineSegment(sketch, "E2.direction2", {"start": v(19.84, -1129.5) * mm, "end": v(19.84, -1091.4) * mm, "construction": true});
            skPoint(sketch, "E3.0.0.57", {"position": v(25.4, 1047.75) * mm});
            skLineSegment(sketch, "E3.1.0.57", {"start": v(19.84, 1053.3) * mm, "end": v(19.84, 1042.2) * mm});
            skLineSegment(sketch, "E3.4.0.57", {"start": v(30.96, 1053.3) * mm, "end": v(30.96, 1042.2) * mm});
            skLineSegment(sketch, "E3.7.0.57", {"start": v(30.96, 1042.2) * mm, "end": v(19.84, 1042.2) * mm});
            skLineSegment(sketch, "E3.10.0.57", {"start": v(30.96, 1053.3) * mm, "end": v(19.84, 1053.3) * mm});
            skPoint(sketch, "E4.0.0.58", {"position": v(25.4, 1085.85) * mm});
            skLineSegment(sketch, "E4.1.0.58", {"start": v(19.84, 1091.4) * mm, "end": v(19.84, 1080.3) * mm});
            skLineSegment(sketch, "E4.4.0.58", {"start": v(30.96, 1091.4) * mm, "end": v(30.96, 1080.3) * mm});
            skLineSegment(sketch, "E4.7.0.58", {"start": v(30.96, 1080.3) * mm, "end": v(19.84, 1080.3) * mm});
            skLineSegment(sketch, "E4.10.0.58", {"start": v(30.96, 1091.4) * mm, "end": v(19.84, 1091.4) * mm});
            skPoint(sketch, "E5.0.0.59", {"position": v(25.4, 1123.95) * mm});
            skLineSegment(sketch, "E5.1.0.59", {"start": v(19.84, 1129.5) * mm, "end": v(19.84, 1118.4) * mm});
            skLineSegment(sketch, "E5.4.0.59", {"start": v(30.96, 1129.5) * mm, "end": v(30.96, 1118.4) * mm});
            skLineSegment(sketch, "E5.7.0.59", {"start": v(30.96, 1118.4) * mm, "end": v(19.84, 1118.4) * mm});
            skLineSegment(sketch, "E5.10.0.59", {"start": v(30.96, 1129.5) * mm, "end": v(19.84, 1129.5) * mm});
            skSolve(sketch);
        }
        {
            var Q0;
            Q0 = qSketchRegion(id + "F3", true);
            extrude(context, id + "F4", {"entities" : qUnion([Q0]), "operationType" : NewBodyOperationType.REMOVE, "endBound" : BoundingType.THROUGH_ALL, "oppositeDirection" : true, "depth" : 25.4 * mm});
        }
    });
